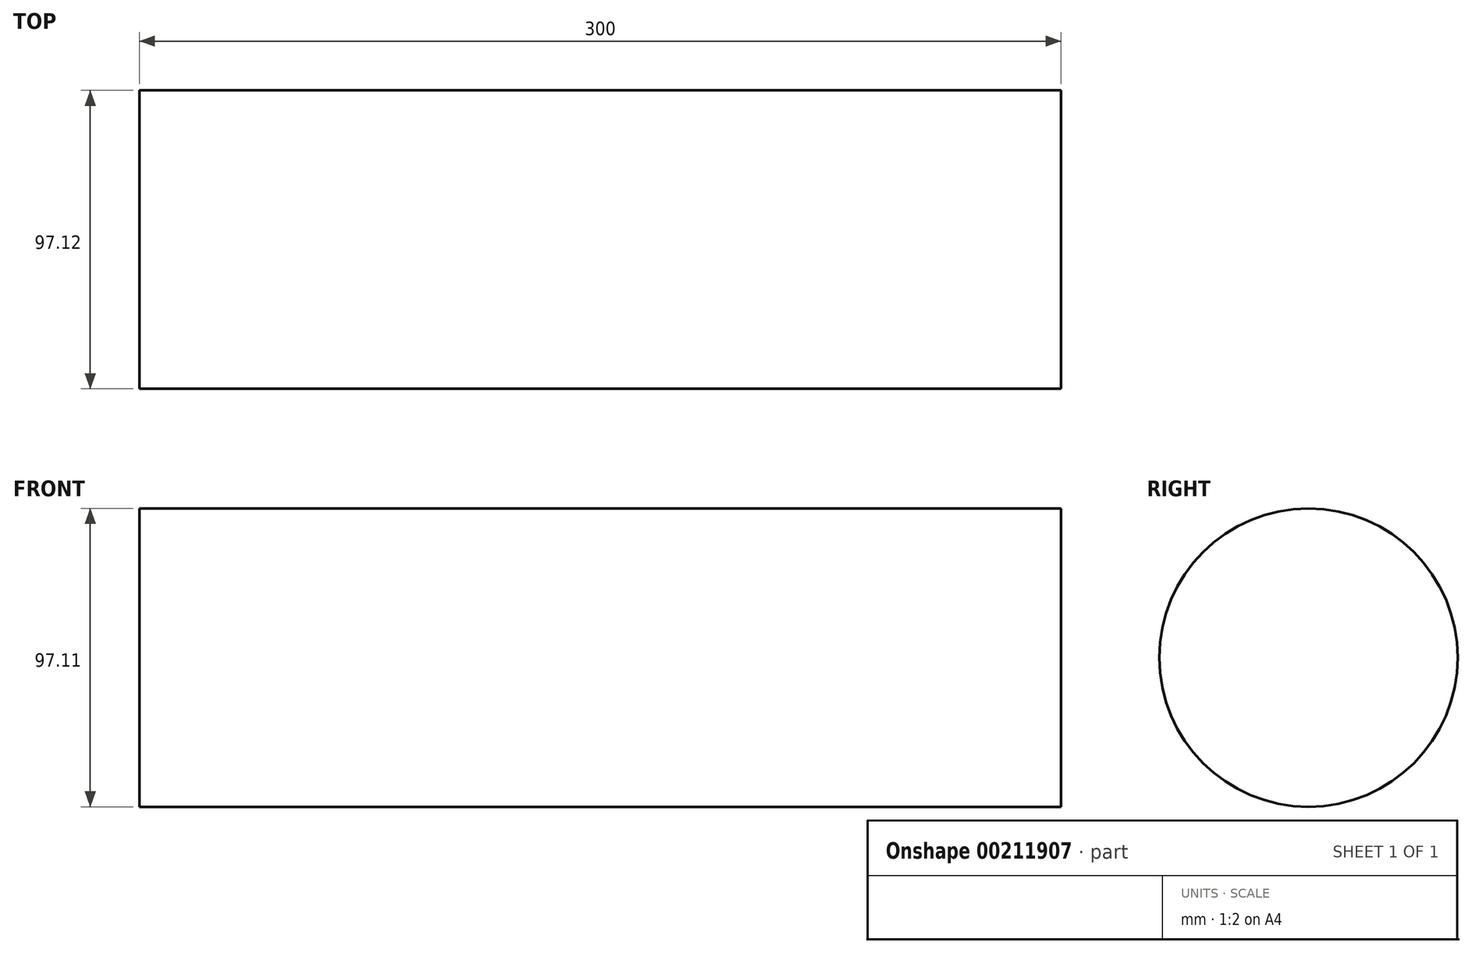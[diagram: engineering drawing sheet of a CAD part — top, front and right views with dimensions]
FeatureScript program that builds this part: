
annotation { "Feature Type Name" : "Feature", "Feature Type Description" : "" }
export const myFeature = defineFeature(function(context is Context, id is Id, definition is map)
    precondition{}
    {
        {
            var Q0;
            Q0=qCreatedBy(makeId("Right.planeOp"),FACE);
            var sketch = newSketch(context, id + "F0", { "sketchPlane" : qUnion([Q0])});
            skLineSegment(sketch, "E0.bottom", {"start": v(-59.4, 22.88) * mm, "end": v(-63.53, 22.88) * mm});
            skLineSegment(sketch, "E0.top", {"start": v(-59.4, 43.43) * mm, "end": v(-63.53, 43.43) * mm});
            skLineSegment(sketch, "E0.left", {"start": v(-59.4, 22.88) * mm, "end": v(-59.4, 43.43) * mm});
            skLineSegment(sketch, "E0.right", {"start": v(-63.53, 22.88) * mm, "end": v(-63.53, 43.43) * mm});
            skCircle(sketch, "E1", {"center": v(-46.5, -57.19) * mm, "radius": 48.56 * mm});
            skSolve(sketch);
        }
        {
            var Q0;
            Q0=makeQuery(id+"F0.imprint","IMPRINT",FACE,{"disambiguationData":[TD([[makeQuery(id+"F0.imprint","IMPRINT",EDGE,{"derivedFrom":sQuery(id+"F0.wireOp",EDGE,"E1")}),1.0]])]});
            extrude(context, id + "F1", {"entities" : qUnion([Q0]), "depth" : 300 * mm});
        }
    });
